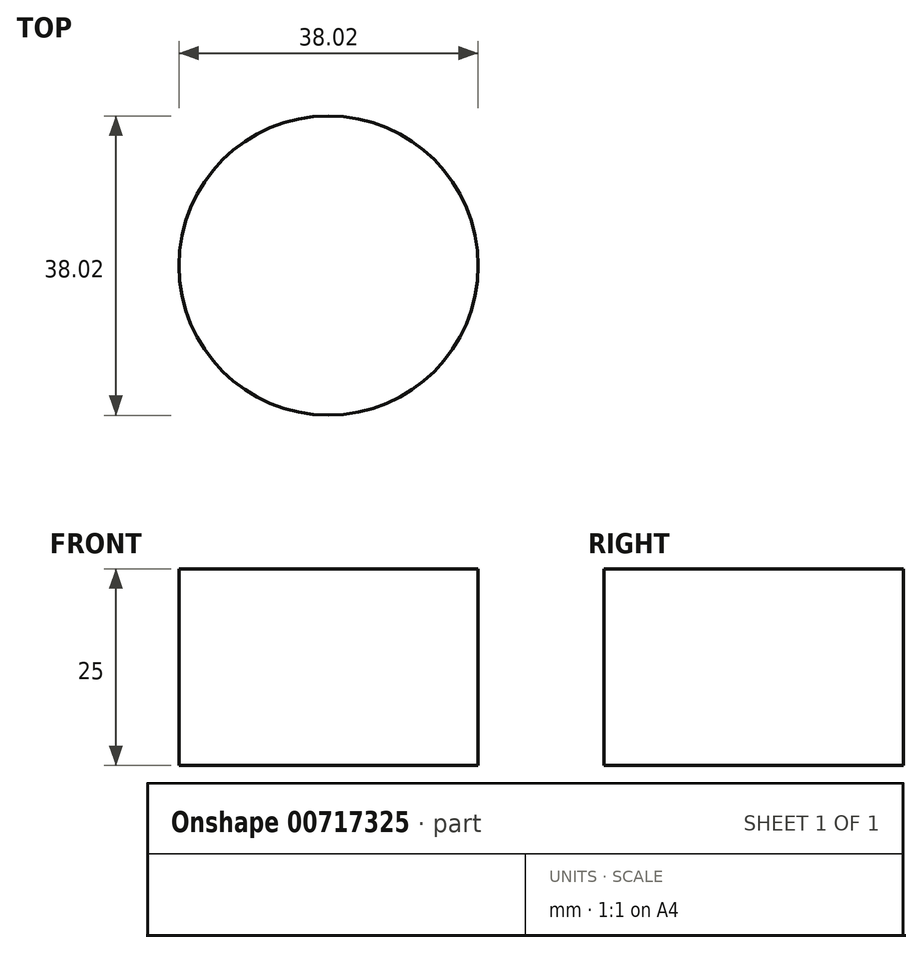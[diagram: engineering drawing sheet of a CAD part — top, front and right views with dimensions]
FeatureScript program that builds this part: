
annotation { "Feature Type Name" : "Feature", "Feature Type Description" : "" }
export const myFeature = defineFeature(function(context is Context, id is Id, definition is map)
    precondition{}
    {
        {
            var Q0;
            Q0=qCreatedBy(makeId("Top.planeOp"),FACE);
            var sketch = newSketch(context, id + "F0", { "sketchPlane" : qUnion([Q0])});
            skCircle(sketch, "E0", {"center": v(0, 0) * mm, "radius": 19 * mm});
            skSolve(sketch);
        }
        {
            var Q0;
            Q0=makeQuery(id+"F0.imprint","IMPRINT",FACE,{"disambiguationData":[TD([[makeQuery(id+"F0.imprint","IMPRINT",EDGE,{"derivedFrom":sQuery(id+"F0.wireOp",EDGE,"E0")}),1.0]])]});
            extrude(context, id + "F1", {"entities" : qUnion([Q0]), "depth" : 25 * mm, "offsetDistance" : 25 * mm});
        }
    });
